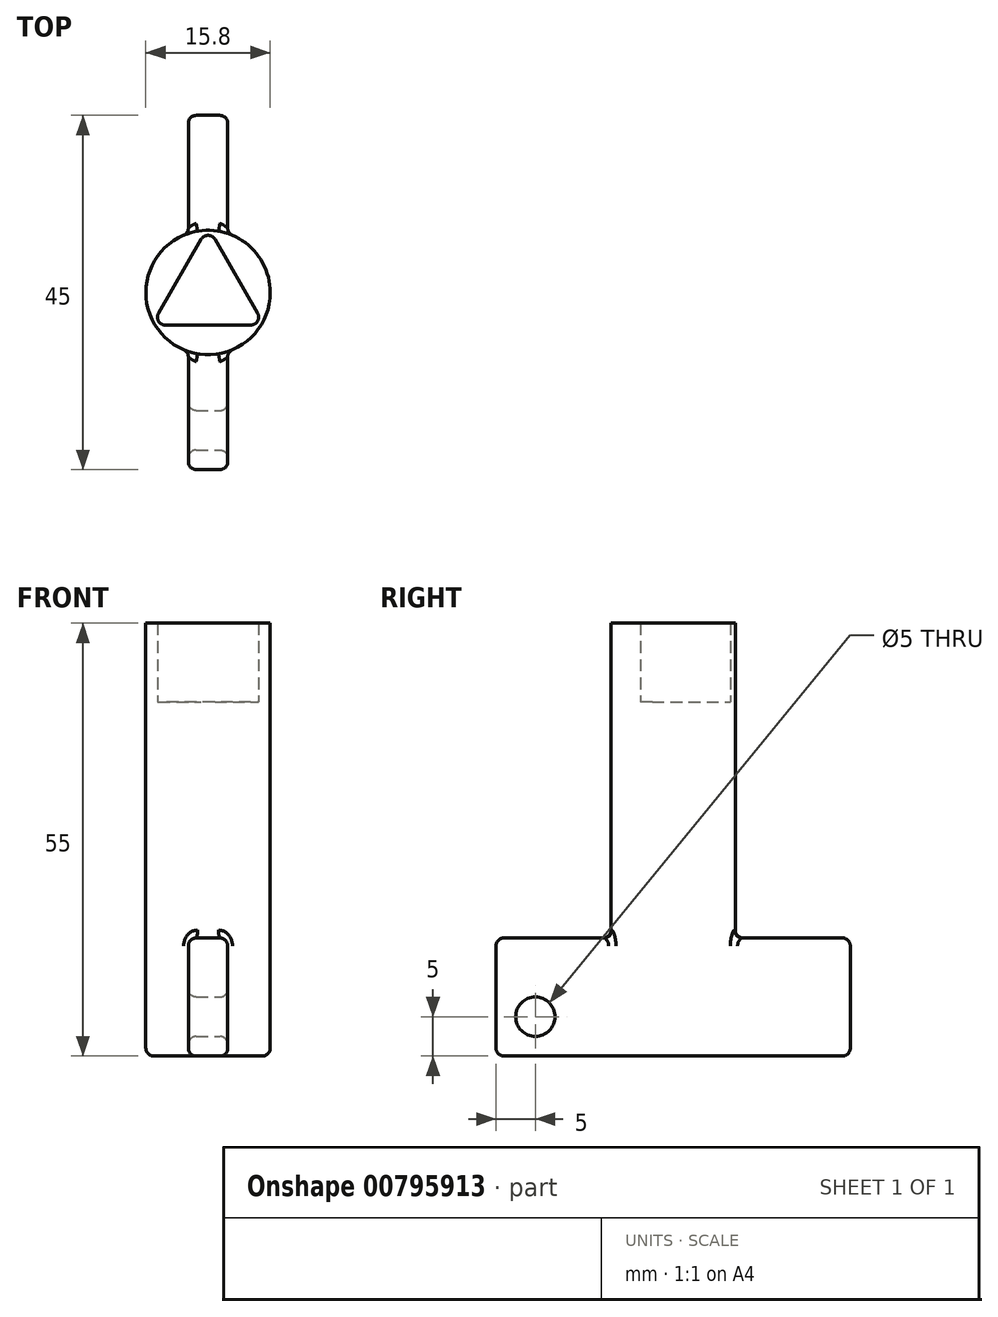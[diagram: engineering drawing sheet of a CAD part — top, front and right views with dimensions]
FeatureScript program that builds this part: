
annotation { "Feature Type Name" : "Feature", "Feature Type Description" : "" }
export const myFeature = defineFeature(function(context is Context, id is Id, definition is map)
    precondition{}
    {
        {
            var Q0;
            Q0=qCreatedBy(makeId("Top.planeOp"),FACE);
            var sketch = newSketch(context, id + "F0", { "sketchPlane" : qUnion([Q0])});
            skCircle(sketch, "E0.cCircle", {"center": v(0, 0) * mm, "radius": 8.27 * mm, "construction": true});
            skLineSegment(sketch, "E0.0", {"start": v(0.87, 6.77) * mm, "end": v(6.3, -2.63) * mm});
            skLineSegment(sketch, "E0.1", {"start": v(5.43, -4.13) * mm, "end": v(-5.43, -4.13) * mm});
            skLineSegment(sketch, "E0.2", {"start": v(-6.3, -2.63) * mm, "end": v(-0.87, 6.77) * mm});
            skCircle(sketch, "E1", {"center": v(0, 0) * mm, "radius": 7.9 * mm});
            skPoint(sketch, "E2.visualSharp", {"position": v(0, 8.27) * mm});
            skArc(sketch, "E2.filletArc", {"start": v(0.87, 6.77) * mm, "mid": v(0, 7.27) * mm, "end": v(-0.87, 6.77) * mm});
            skPoint(sketch, "E3.visualSharp", {"position": v(-7.16, -4.13) * mm});
            skArc(sketch, "E3.filletArc", {"start": v(-6.3, -2.63) * mm, "mid": v(-6.3, -3.63) * mm, "end": v(-5.43, -4.13) * mm});
            skPoint(sketch, "E4.visualSharp", {"position": v(7.16, -4.13) * mm});
            skArc(sketch, "E4.filletArc", {"start": v(5.43, -4.13) * mm, "mid": v(6.3, -3.63) * mm, "end": v(6.3, -2.63) * mm});
            skSolve(sketch);
        }
        {
            var Q0;
            Q0 = qSketchRegion(id + "F0", true);
            extrude(context, id + "F1", {"entities" : qUnion([Q0]), "depth" : 10 * mm, "offsetDistance" : 25 * mm});
        }
        {
            var Q0;
            Q0=qCreatedBy(makeId("Top.planeOp"),FACE);
            var sketch = newSketch(context, id + "F2", { "sketchPlane" : qUnion([Q0])});
            skCircle(sketch, "E5", {"center": v(0, 0) * mm, "radius": 7.9 * mm});
            skSolve(sketch);
        }
        {
            var Q0;
            Q0 = qSketchRegion(id + "F2", true);
            extrude(context, id + "F3", {"entities" : qUnion([Q0]), "operationType" : NewBodyOperationType.ADD, "oppositeDirection" : true, "depth" : 45 * mm, "offsetDistance" : 25 * mm});
        }
        {
            var Q0;
            Q0=makeQuery(id+"F3.opExtrude","CAP_FACE",FACE,{"disambiguationData":[OSD([sQuery(id+"F2.wireOp",EDGE,"E5")])],"isStart":false});
            var sketch = newSketch(context, id + "F4", { "sketchPlane" : qUnion([Q0])});
            skLineSegment(sketch, "E6.bottom", {"start": v(-2.5, -22.5) * mm, "end": v(2.5, -22.5) * mm});
            skLineSegment(sketch, "E6.top", {"start": v(-2.5, 22.5) * mm, "end": v(2.5, 22.5) * mm});
            skLineSegment(sketch, "E6.left", {"start": v(-2.5, -22.5) * mm, "end": v(-2.5, 22.5) * mm});
            skLineSegment(sketch, "E6.right", {"start": v(2.5, -22.5) * mm, "end": v(2.5, 22.5) * mm});
            skSolve(sketch);
        }
        {
            var Q0;
            {var subQ0=sQuery(id+"F4.wireOp",EDGE,"E6.bottom");Q0=makeQuery(id+"F4.imprint","IMPRINT",FACE,{"disambiguationData":[TD([[makeQuery(id+"F4.imprint","IMPRINT",EDGE,{"derivedFrom":subQ0}),1.0]])]});}
            var Q1;
            {var subQ0=sQuery(id+"F4.wireOp",EDGE,"E6.left");var subQ1=makeQuery(id+"F3.opExtrude","CAP_EDGE",EDGE,{"disambiguationData":[OSD([sQuery(id+"F2.wireOp",EDGE,"E5")])],"isStart":false});var subQ2=makeQuery(id+"F4.imprint","INTERSECT",VERTEX,{"disambiguationData":[OD(0.0)],"derivedFrom":[subQ1,subQ0]});Q1=makeQuery(id+"F4.imprint","IMPRINT",FACE,{"disambiguationData":[TD([[makeQuery(id+"F4.imprint","IMPRINT",EDGE,{"disambiguationData":[TD([[subQ2,-1.0]])],"derivedFrom":subQ0}),-1.0]])]});}
            var Q2;
            {var subQ0=sQuery(id+"F4.wireOp",EDGE,"E6.top");Q2=makeQuery(id+"F4.imprint","IMPRINT",FACE,{"disambiguationData":[TD([[makeQuery(id+"F4.imprint","IMPRINT",EDGE,{"derivedFrom":subQ0}),-1.0]])]});}
            extrude(context, id + "F5", {"entities" : qUnion([Q0, Q1, Q2]), "operationType" : NewBodyOperationType.ADD, "oppositeDirection" : true, "depth" : 15 * mm, "offsetDistance" : 25 * mm});
        }
        {
            var Q0;
            {var subQ1=sQuery(id+"F4.wireOp",EDGE,"E6.left");var subQ2=sQuery(id+"F4.wireOp",EDGE,"E6.top");Q0=makeQuery(id+"F5.boolean.opBoolean","SPLIT",FACE,{"disambiguationData":[TD([makeQuery(id+"F5.opExtrude","SWEPT_FACE",FACE,{"disambiguationData":[OSD([subQ2])]})])],"derivedFrom":makeQuery(id+"F5.opExtrude","SWEPT_FACE",FACE,{"disambiguationData":[OSD([subQ1])]})});}
            var sketch = newSketch(context, id + "F6", { "sketchPlane" : qUnion([Q0])});
            skLineSegment(sketch, "E7", {"start": v(17.5, -45) * mm, "end": v(17.5, -40) * mm, "construction": true});
            skSolve(sketch);
        }
        {
            var Q0;
            Q0=sQuery(id+"F6.wireOp",VERTEX,"E7.end");
            var Q1;
            Q1=makeQuery(id+"F1.opExtrude","SWEPT_BODY",BODY,{"disambiguationData":[OSD([sQuery(id+"F0.wireOp",EDGE,"E0.0"),sQuery(id+"F0.wireOp",EDGE,"E0.1"),sQuery(id+"F0.wireOp",EDGE,"E0.2"),sQuery(id+"F0.wireOp",EDGE,"E1"),sQuery(id+"F0.wireOp",EDGE,"E2.filletArc"),sQuery(id+"F0.wireOp",EDGE,"E3.filletArc"),sQuery(id+"F0.wireOp",EDGE,"E4.filletArc")])]});
            hole(context, id + "F7", {"style" : HoleStyle.SIMPLE, "endStyle" : HoleEndStyle.THROUGH, "holeDiameter" : 5 * mm, "majorDiameter" : 5 * mm, "isTappedThrough" : true, "tappedDepth" : 12 * mm, "tapClearance" : 3, "locations" : qUnion([Q0]), "scope" : qUnion([Q1])});
        }
        {
            var Q0;
            {var subQ0=sQuery(id+"F4.wireOp",EDGE,"E6.left");var subQ1=sQuery(id+"F4.wireOp",EDGE,"E6.bottom");var subQ2=sQuery(id+"F4.wireOp",EDGE,"E6.right");Q0=makeQuery(id+"F5.boolean.opBoolean","SPLIT",FACE,{"disambiguationData":[TD([makeQuery(id+"F5.opExtrude","SWEPT_FACE",FACE,{"disambiguationData":[OSD([subQ1])]})])],"derivedFrom":makeQuery(id+"F5.opExtrude","CAP_FACE",FACE,{"disambiguationData":[OSD([subQ1,sQuery(id+"F4.wireOp",EDGE,"E6.top"),subQ0,subQ2])],"isStart":false})});}
            var Q1;
            {var subQ0=sQuery(id+"F4.wireOp",EDGE,"E6.left");var subQ1=sQuery(id+"F4.wireOp",EDGE,"E6.top");var subQ2=sQuery(id+"F4.wireOp",EDGE,"E6.right");Q1=makeQuery(id+"F5.boolean.opBoolean","SPLIT",FACE,{"disambiguationData":[TD([makeQuery(id+"F5.opExtrude","SWEPT_FACE",FACE,{"disambiguationData":[OSD([subQ1])]})])],"derivedFrom":makeQuery(id+"F5.opExtrude","CAP_FACE",FACE,{"disambiguationData":[OSD([sQuery(id+"F4.wireOp",EDGE,"E6.bottom"),subQ1,subQ0,subQ2])],"isStart":false})});}
            var Q2;
            Q2=makeQuery(id+"F5.boolean.opBoolean","MERGE",FACE,{"derivedFrom":[makeQuery(id+"F3.opExtrude","CAP_FACE",FACE,{"disambiguationData":[OSD([sQuery(id+"F2.wireOp",EDGE,"E5")])],"isStart":false}),makeQuery(id+"F5.opExtrude","CAP_FACE",FACE,{"disambiguationData":[OSD([sQuery(id+"F4.wireOp",EDGE,"E6.bottom"),sQuery(id+"F4.wireOp",EDGE,"E6.top"),sQuery(id+"F4.wireOp",EDGE,"E6.left"),sQuery(id+"F4.wireOp",EDGE,"E6.right")])],"isStart":true})]});
            var Q3;
            {var subQ0=sQuery(id+"F4.wireOp",EDGE,"E6.right");var subQ2=sQuery(id+"F4.wireOp",EDGE,"E6.top");Q3=makeQuery(id+"F5.boolean.opBoolean","SPLIT",FACE,{"disambiguationData":[TD([makeQuery(id+"F5.opExtrude","SWEPT_FACE",FACE,{"disambiguationData":[OSD([subQ2])]})])],"derivedFrom":makeQuery(id+"F5.opExtrude","SWEPT_FACE",FACE,{"disambiguationData":[OSD([subQ0])]})});}
            var Q4;
            {var subQ0=sQuery(id+"F4.wireOp",EDGE,"E6.bottom");var subQ2=sQuery(id+"F4.wireOp",EDGE,"E6.right");Q4=makeQuery(id+"F5.boolean.opBoolean","SPLIT",FACE,{"disambiguationData":[TD([makeQuery(id+"F5.opExtrude","SWEPT_FACE",FACE,{"disambiguationData":[OSD([subQ0])]})])],"derivedFrom":makeQuery(id+"F5.opExtrude","SWEPT_FACE",FACE,{"disambiguationData":[OSD([subQ2])]})});}
            var Q5;
            {var subQ0=sQuery(id+"F4.wireOp",EDGE,"E6.bottom");var subQ3=sQuery(id+"F4.wireOp",EDGE,"E6.left");Q5=makeQuery(id+"F5.boolean.opBoolean","SPLIT",FACE,{"disambiguationData":[TD([makeQuery(id+"F5.opExtrude","SWEPT_FACE",FACE,{"disambiguationData":[OSD([subQ0])]})])],"derivedFrom":makeQuery(id+"F5.opExtrude","SWEPT_FACE",FACE,{"disambiguationData":[OSD([subQ3])]})});}
            var Q6;
            {var subQ1=sQuery(id+"F4.wireOp",EDGE,"E6.left");var subQ2=sQuery(id+"F4.wireOp",EDGE,"E6.top");Q6=makeQuery(id+"F5.boolean.opBoolean","SPLIT",FACE,{"disambiguationData":[TD([makeQuery(id+"F5.opExtrude","SWEPT_FACE",FACE,{"disambiguationData":[OSD([subQ2])]})])],"derivedFrom":makeQuery(id+"F5.opExtrude","SWEPT_FACE",FACE,{"disambiguationData":[OSD([subQ1])]})});}
            fillet(context, id + "F8", {"entities" : qUnion([Q0, Q1, Q2, Q3, Q4, Q5, Q6]), "radius" : 1 * mm, "tangentPropagation" : true, "allowEdgeOverflow" : false});
        }
    });
